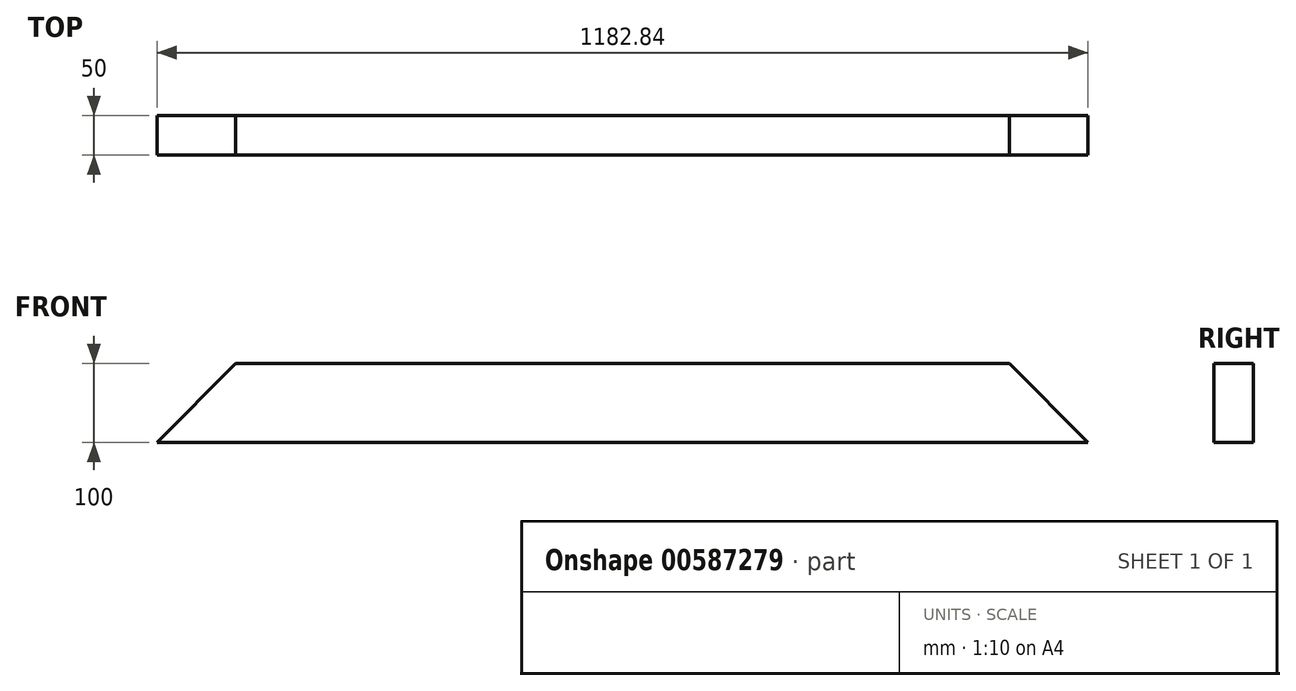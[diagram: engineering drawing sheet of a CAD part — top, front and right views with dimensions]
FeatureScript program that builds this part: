
annotation { "Feature Type Name" : "Feature", "Feature Type Description" : "" }
export const myFeature = defineFeature(function(context is Context, id is Id, definition is map)
    precondition{}
    {
        {
            var Q0;
            Q0=qCreatedBy(makeId("Front.planeOp"),FACE);
            var sketch = newSketch(context, id + "F0", { "sketchPlane" : qUnion([Q0])});
            skLineSegment(sketch, "E0", {"start": v(-1250, 0) * mm, "end": v(1250, 0) * mm, "construction": true});
            skLineSegment(sketch, "E1", {"start": v(1250, 0) * mm, "end": v(0, 1250) * mm, "construction": true});
            skLineSegment(sketch, "E2", {"start": v(0, 1250) * mm, "end": v(-1250, 0) * mm, "construction": true});
            skLineSegment(sketch, "E3", {"start": v(0, 1250) * mm, "end": v(-141.42, 1250) * mm, "construction": true});
            skLineSegment(sketch, "E4", {"start": v(-1250, 0) * mm, "end": v(-1391.42, 0) * mm, "construction": true});
            skLineSegment(sketch, "E5", {"start": v(-1391.42, 0) * mm, "end": v(-141.42, 1250) * mm, "construction": true});
            skLineSegment(sketch, "E6", {"start": v(-491.42, 900) * mm, "end": v(491.42, 900) * mm});
            skLineSegment(sketch, "E7", {"start": v(-491.42, 900) * mm, "end": v(-591.42, 800) * mm});
            skLineSegment(sketch, "E8", {"start": v(-591.42, 800) * mm, "end": v(591.42, 800) * mm});
            skLineSegment(sketch, "E9", {"start": v(591.42, 800) * mm, "end": v(491.42, 900) * mm});
            skPoint(sketch, "E10", {"position": v(0, 800) * mm});
            skPoint(sketch, "E11", {"position": v(0, 900) * mm});
            skSolve(sketch);
        }
        {
            var Q0;
            Q0=makeQuery(id+"F0.imprint","IMPRINT",FACE,{"disambiguationData":[TD([[makeQuery(id+"F0.imprint","IMPRINT",EDGE,{"derivedFrom":sQuery(id+"F0.wireOp",EDGE,"E6")}),-1.0]])]});
            extrude(context, id + "F1", {"entities" : qUnion([Q0]), "depth" : 50 * mm, "offsetDistance" : 25 * mm});
        }
    });
